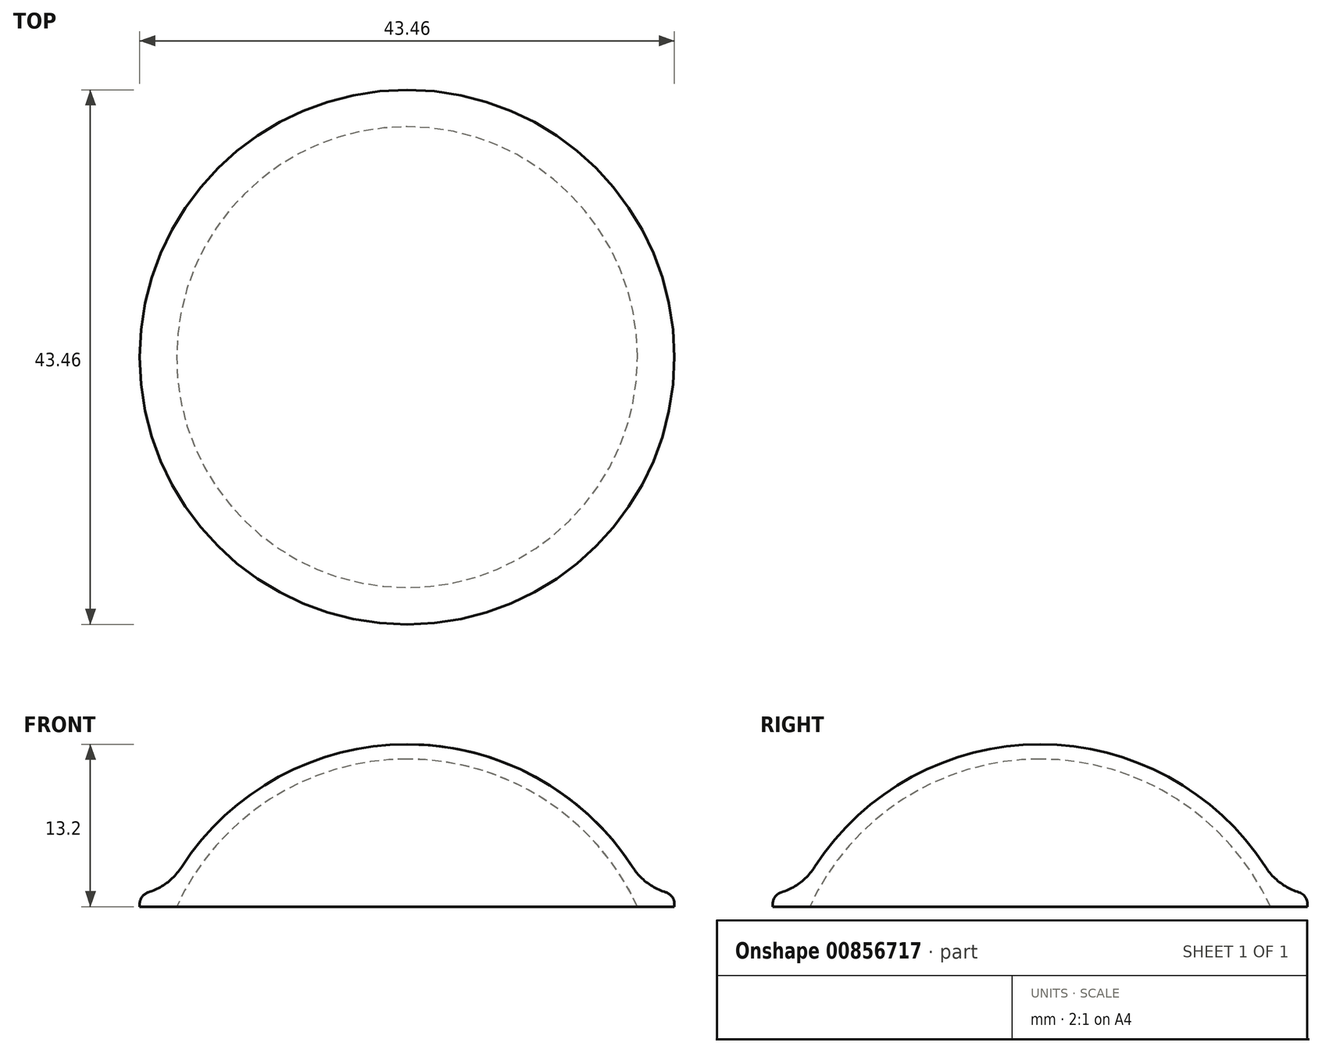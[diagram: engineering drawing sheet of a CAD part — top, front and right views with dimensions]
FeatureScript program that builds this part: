
annotation { "Feature Type Name" : "Feature", "Feature Type Description" : "" }
export const myFeature = defineFeature(function(context is Context, id is Id, definition is map)
    precondition{}
    {
        {
            var Q0;
            Q0=qCreatedBy(makeId("Front.planeOp"),FACE);
            var sketch = newSketch(context, id + "F0", { "sketchPlane" : qUnion([Q0])});
            skLineSegment(sketch, "E0", {"start": v(0, 0) * mm, "end": v(18.73, 0) * mm});
            skLineSegment(sketch, "E1", {"start": v(18.73, 0) * mm, "end": v(21.73, 0) * mm});
            skLineSegment(sketch, "E2", {"start": v(21.73, 0) * mm, "end": v(21.73, 1) * mm});
            skLineSegment(sketch, "E3", {"start": v(21.73, 1) * mm, "end": v(19.73, 1) * mm});
            skArc(sketch, "E4", {"start": v(18.73, 0) * mm, "mid": v(11.12, 8.74) * mm, "end": v(0, 12) * mm});
            skArc(sketch, "E5.0", {"start": v(19.59, 1) * mm, "mid": v(11.54, 9.9) * mm, "end": v(0, 13.2) * mm});
            skPoint(sketch, "E6", {"position": v(19.59, 1) * mm});
            skLineSegment(sketch, "E7", {"start": v(19.73, 1) * mm, "end": v(19.59, 1) * mm});
            skLineSegment(sketch, "E8", {"start": v(0, 13.2) * mm, "end": v(0, 12) * mm});
            skSolve(sketch);
        }
        {
            var Q0;
            Q0 = qSketchRegion(id + "F0", true);
            var Q1;
            Q1=sQuery(id+"F0.wireOp",EDGE,"E8");
            revolve(context, id + "F1", {"surfaceOperationType" : NewSurfaceOperationType.NEW, "entities" : qUnion([Q0]), "axis" : qUnion([Q1]), "revolveType" : RevolveType.FULL});
        }
        {
            var Q0;
            Q0=makeQuery(id+"F1.opRevolve","SWEPT_EDGE",EDGE,{"disambiguationData":[OSD([sQuery(id+"F0.wireOp",EDGE,"E5.0"),sQuery(id+"F0.wireOp",EDGE,"E7")])]});
            fillet(context, id + "F2", {"entities" : qUnion([Q0]), "radius" : 5 * mm, "tangentPropagation" : true, "allowEdgeOverflow" : false});
        }
        {
            var Q0;
            Q0=makeQuery(id+"F1.opRevolve","SWEPT_EDGE",EDGE,{"disambiguationData":[OSD([sQuery(id+"F0.wireOp",EDGE,"E2"),sQuery(id+"F0.wireOp",EDGE,"E3")])]});
            var Q1;
            Q1=makeQuery(id+"F2.opFillet","BLEND_EDGE",EDGE,{"blendedFrom":[makeQuery(id+"F1.opRevolve","SWEPT_EDGE",EDGE,{"disambiguationData":[OSD([sQuery(id+"F0.wireOp",EDGE,"E5.0"),sQuery(id+"F0.wireOp",EDGE,"E7")])]}),makeQuery(id+"F1.opRevolve","SWEPT_FACE",FACE,{"disambiguationData":[OSD([sQuery(id+"F0.wireOp",EDGE,"E2")])]})],"blendedInto":[makeQuery(id+"F1.opRevolve","SWEPT_FACE",FACE,{"disambiguationData":[OSD([sQuery(id+"F0.wireOp",EDGE,"E2")])]})]});
            fillet(context, id + "F3", {"entities" : qUnion([Q0, Q1]), "radius" : 1 * mm, "tangentPropagation" : true, "allowEdgeOverflow" : false});
        }
    });
